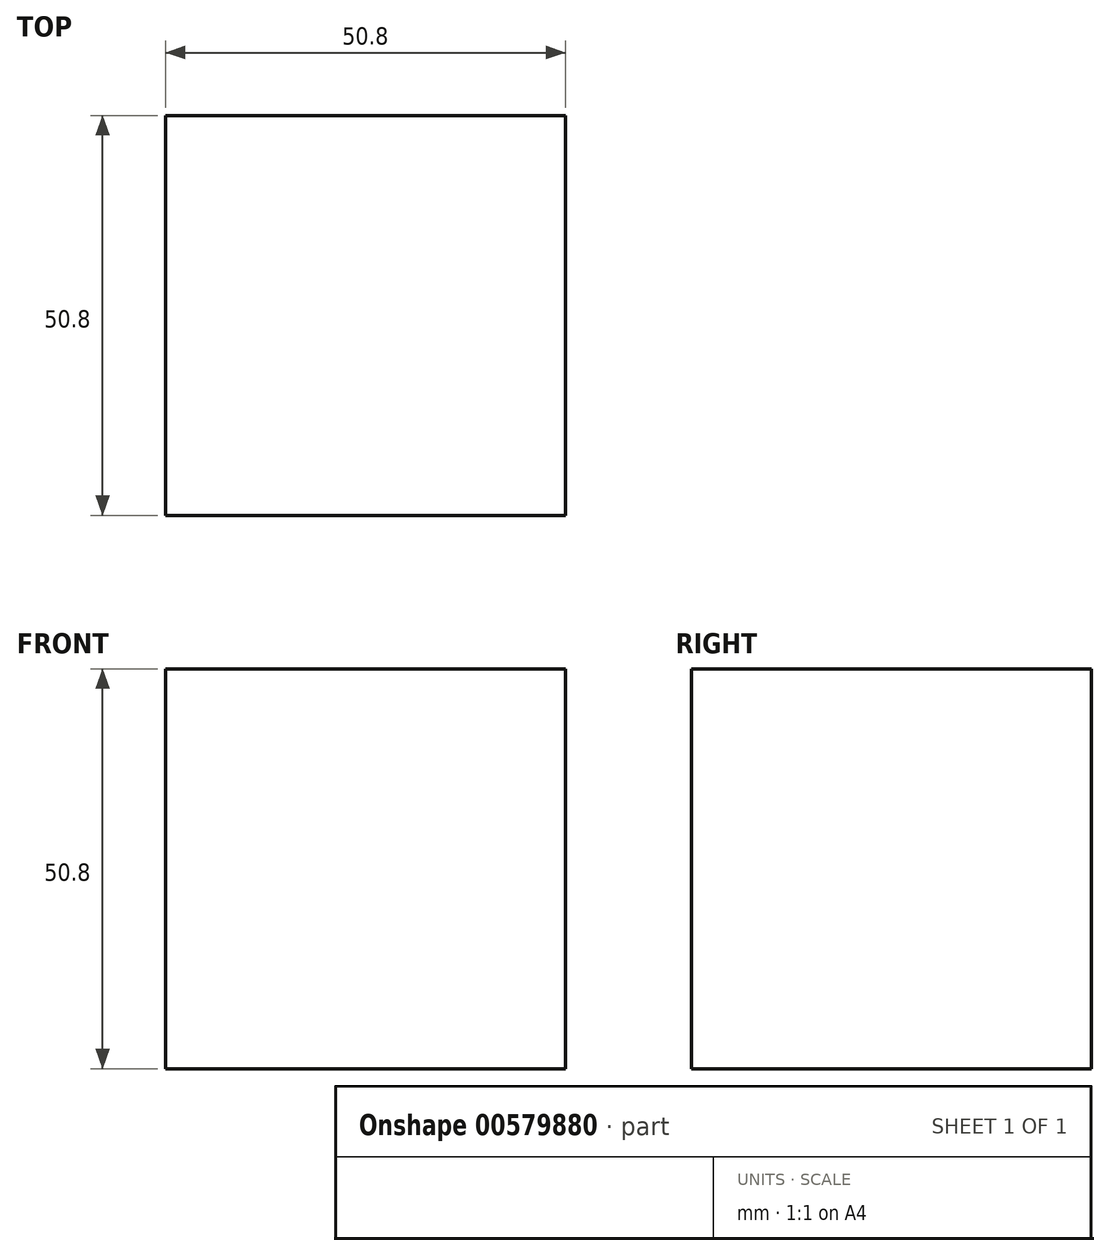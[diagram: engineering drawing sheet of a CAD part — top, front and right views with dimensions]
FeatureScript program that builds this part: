
annotation { "Feature Type Name" : "Feature", "Feature Type Description" : "" }
export const myFeature = defineFeature(function(context is Context, id is Id, definition is map)
    precondition{}
    {
        {
            var Q0;
            Q0=qCreatedBy(makeId("Front.planeOp"),FACE);
            var sketch = newSketch(context, id + "F0", { "sketchPlane" : qUnion([Q0])});
            skLineSegment(sketch, "E0.bottom", {"start": v(0, 0) * mm, "end": v(50.8, 0) * mm});
            skLineSegment(sketch, "E0.top", {"start": v(0, 50.8) * mm, "end": v(50.8, 50.8) * mm});
            skLineSegment(sketch, "E0.left", {"start": v(0, 0) * mm, "end": v(0, 50.8) * mm});
            skLineSegment(sketch, "E0.right", {"start": v(50.8, 0) * mm, "end": v(50.8, 50.8) * mm});
            skSolve(sketch);
        }
        {
            var Q0;
            Q0=makeQuery(id+"F0.imprint","IMPRINT",FACE,{"disambiguationData":[TD([[makeQuery(id+"F0.imprint","IMPRINT",EDGE,{"derivedFrom":sQuery(id+"F0.wireOp",EDGE,"E0.bottom")}),1.0]])]});
            extrude(context, id + "F1", {"entities" : qUnion([Q0]), "depth" : 50.8 * mm, "offsetDistance" : 25.4 * mm});
        }
    });
